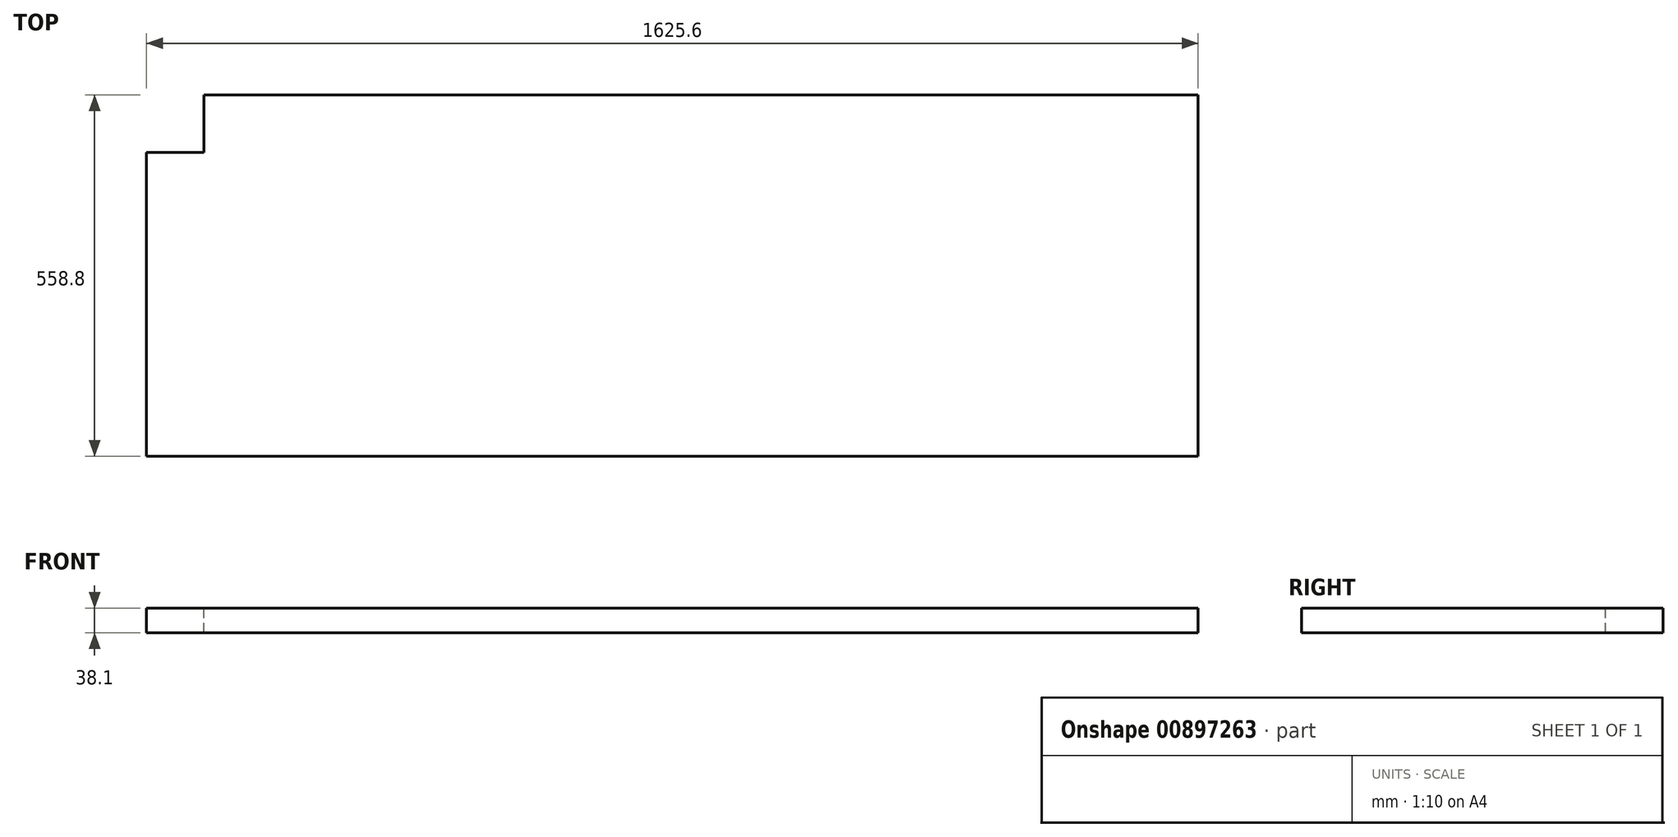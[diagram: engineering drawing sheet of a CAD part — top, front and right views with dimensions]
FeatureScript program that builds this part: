
annotation { "Feature Type Name" : "Feature", "Feature Type Description" : "" }
export const myFeature = defineFeature(function(context is Context, id is Id, definition is map)
    precondition{}
    {
        {
            var Q0;
            Q0=qCreatedBy(makeId("Top.planeOp"),FACE);
            var sketch = newSketch(context, id + "F0", { "sketchPlane" : qUnion([Q0])});
            skLineSegment(sketch, "E0.bottom", {"start": v(-812.8, 279.4) * mm, "end": v(812.8, 279.4) * mm});
            skLineSegment(sketch, "E0.top", {"start": v(-812.8, -279.4) * mm, "end": v(812.8, -279.4) * mm});
            skLineSegment(sketch, "E0.left", {"start": v(-812.8, 279.4) * mm, "end": v(-812.8, -279.4) * mm});
            skLineSegment(sketch, "E0.right", {"start": v(812.8, 279.4) * mm, "end": v(812.8, -279.4) * mm});
            skPoint(sketch, "E0.middle", {"position": v(0, 0) * mm});
            skSolve(sketch);
        }
        {
            var Q0;
            Q0=makeQuery(id+"F0.imprint","IMPRINT",FACE,{"disambiguationData":[TD([[makeQuery(id+"F0.imprint","IMPRINT",EDGE,{"derivedFrom":sQuery(id+"F0.wireOp",EDGE,"E0.bottom")}),-1.0]])]});
            extrude(context, id + "F1", {"entities" : qUnion([Q0]), "depth" : 38.1 * mm, "offsetDistance" : 25.4 * mm});
        }
        {
            var Q0;
            Q0=makeQuery(id+"F1.opExtrude","CAP_FACE",FACE,{"disambiguationData":[OSD([sQuery(id+"F0.wireOp",EDGE,"E0.bottom"),sQuery(id+"F0.wireOp",EDGE,"E0.top"),sQuery(id+"F0.wireOp",EDGE,"E0.left"),sQuery(id+"F0.wireOp",EDGE,"E0.right")])],"isStart":false});
            var sketch = newSketch(context, id + "F2", { "sketchPlane" : qUnion([Q0])});
            skLineSegment(sketch, "E1.bottom", {"start": v(-812.8, 279.4) * mm, "end": v(-723.9, 279.4) * mm});
            skLineSegment(sketch, "E1.top", {"start": v(-812.8, 190.5) * mm, "end": v(-723.9, 190.5) * mm});
            skLineSegment(sketch, "E1.left", {"start": v(-812.8, 279.4) * mm, "end": v(-812.8, 190.5) * mm});
            skLineSegment(sketch, "E1.right", {"start": v(-723.9, 279.4) * mm, "end": v(-723.9, 190.5) * mm});
            skSolve(sketch);
        }
        {
            var Q0;
            Q0=makeQuery(id+"F2.imprint","IMPRINT",FACE,{"disambiguationData":[TD([[makeQuery(id+"F2.imprint","IMPRINT",EDGE,{"derivedFrom":sQuery(id+"F2.wireOp",EDGE,"E1.bottom")}),-1.0]])]});
            var Q1;
            Q1=makeQuery(id+"F2.imprint","IMPRINT",FACE,{"disambiguationData":[TD([[makeQuery(id+"F2.imprint","IMPRINT",EDGE,{"derivedFrom":sQuery(id+"F2.wireOp",EDGE,"GDQuSk3S-R5L9-dQjB-DJjh-Hf5p5fPP3tp5.bottom")}),1.0]])]});
            extrude(context, id + "F3", {"entities" : qUnion([Q0, Q1]), "operationType" : NewBodyOperationType.REMOVE, "endBound" : BoundingType.THROUGH_ALL, "oppositeDirection" : true, "depth" : 25.4 * mm, "offsetDistance" : 25.4 * mm});
        }
    });
